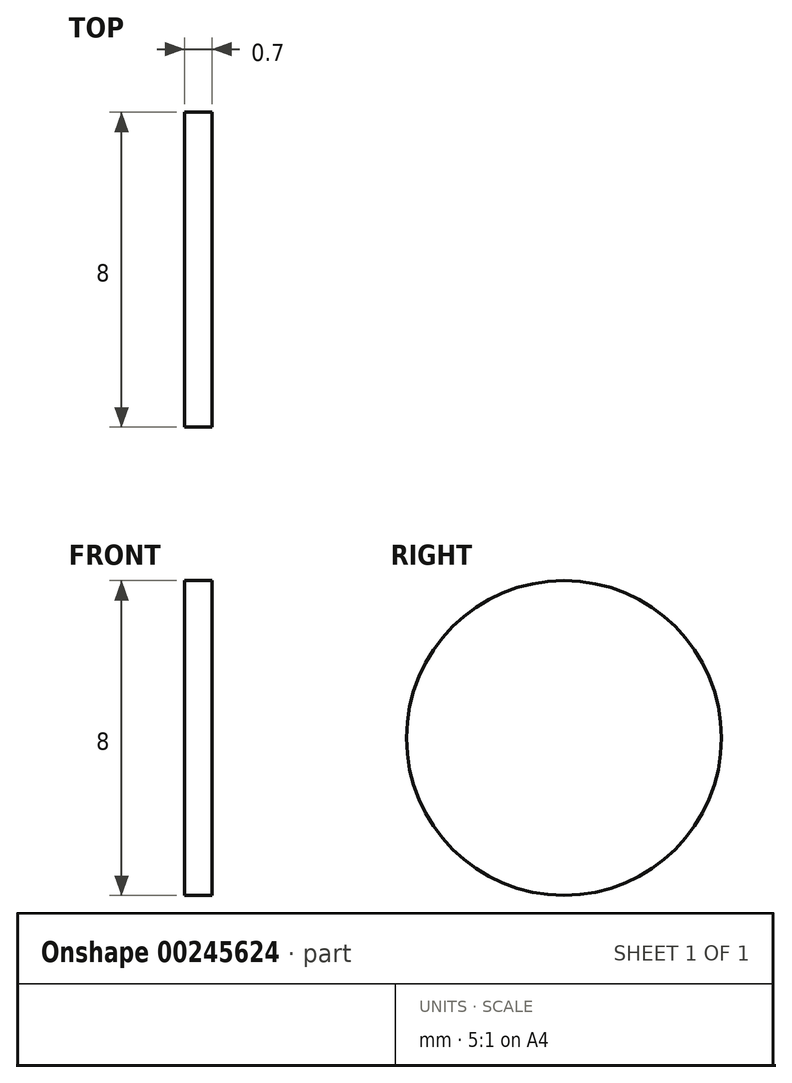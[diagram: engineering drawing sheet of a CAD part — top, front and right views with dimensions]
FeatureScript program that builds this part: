
annotation { "Feature Type Name" : "Feature", "Feature Type Description" : "" }
export const myFeature = defineFeature(function(context is Context, id is Id, definition is map)
    precondition{}
    {
        {
            var Q0;
            Q0=qCreatedBy(makeId("Right.planeOp"),FACE);
            var sketch = newSketch(context, id + "F0", { "sketchPlane" : qUnion([Q0])});
            skCircle(sketch, "E0", {"center": v(0, 0) * mm, "radius": 4 * mm});
            skSolve(sketch);
        }
        {
            var Q0;
            Q0=makeQuery(id+"F0.imprint","IMPRINT",FACE,{"disambiguationData":[TD([[makeQuery(id+"F0.imprint","IMPRINT",EDGE,{"derivedFrom":sQuery(id+"F0.wireOp",EDGE,"E0")}),1.0]])]});
            extrude(context, id + "F1", {"entities" : qUnion([Q0]), "depth" : 0.7 * mm});
        }
    });
